FCSTD DOCUMENT  (FreeCAD 0.19R23546 (Git))
Label: PCB Reference
License: All rights reserved
LicenseURL: http://en.wikipedia.org/wiki/All_rights_reserved
objects: TechDraw::DrawViewDimension×22, TechDraw::DrawRichAnno×22, Spreadsheet::Sheet×1, Sketcher::SketchObject×1, PartDesign::Body×1, TechDraw::DrawSVGTemplate×1, TechDraw::DrawViewPart×1, TechDraw::DrawPage×1
note: 2 computed .brp shape members not serialized (recipe doc carries the construction recipe); baked Part::Feature solids carry a one-line shape summary decoded from their .brp

FEATURE [Spreadsheet::Sheet] Spreadsheet  label="Variables"
FEATURE [Sketcher::SketchObject] Sketch
  MapMode = 5
  Support = -> [XY_Plane]
  sketch-geometry (34):
    g0: LineSegment StartX=-33 StartY=-8.93934 StartZ=0 EndX=-31.9393 EndY=-10 EndZ=0
    g1: LineSegment StartX=-31.9393 StartY=-10 StartZ=0 EndX=31.9393 EndY=-10 EndZ=0
    g2: LineSegment StartX=31.9393 StartY=-10 StartZ=0 EndX=33 EndY=-8.93934 EndZ=0
    g3: LineSegment StartX=-33 StartY=-8.93934 StartZ=0 EndX=-33 EndY=6.93934 EndZ=0
    g4: LineSegment StartX=-33 StartY=6.93934 StartZ=0 EndX=-31.9393 EndY=8 EndZ=0
    g5: LineSegment StartX=33 StartY=-8.93934 StartZ=0 EndX=33 EndY=-2.56066 EndZ=0
    g6: LineSegment StartX=33 StartY=-2.56066 StartZ=0 EndX=31.9393 EndY=-1.5 EndZ=0
    g7: LineSegment StartX=-31.9393 StartY=8 StartZ=0 EndX=-28 EndY=8 EndZ=0
    g8: LineSegment StartX=24.9393 StartY=6.5 StartZ=0 EndX=-16 EndY=6.5 EndZ=0
    g9: LineSegment StartX=-16 StartY=6.5 StartZ=0 EndX=-19.5 EndY=10 EndZ=0
    g10: LineSegment StartX=-19.5 StartY=10 StartZ=0 EndX=-26 EndY=10 EndZ=0
    g11: LineSegment StartX=-26 StartY=10 StartZ=0 EndX=-28 EndY=8 EndZ=0
    g12: LineSegment StartX=24.9393 StartY=6.5 StartZ=0 EndX=26 EndY=5.43934 EndZ=0
    g13: LineSegment StartX=31.9393 StartY=-1.5 StartZ=0 EndX=26 EndY=-1.5 EndZ=0
    g14: LineSegment StartX=26 StartY=-1.5 StartZ=0 EndX=26 EndY=5.43934 EndZ=0
    g15: GeomPoint X=-19.5 Y=-10 Z=0
    g16: Circle CenterX=-29 CenterY=-5 CenterZ=0 NormalX=0 NormalY=0 NormalZ=1 AngleXU=0 Radius=2
    g17: Circle CenterX=29 CenterY=-5 CenterZ=0 NormalX=0 NormalY=0 NormalZ=1 AngleXU=0 Radius=2
    g18: LineSegment StartX=-32 StartY=5.5 StartZ=0 EndX=-26 EndY=5.5 EndZ=0
    g19: LineSegment StartX=-26 StartY=5.5 StartZ=0 EndX=-26 EndY=-0.5 EndZ=0
    g20: LineSegment StartX=-26 StartY=-0.5 StartZ=0 EndX=-32 EndY=-0.5 EndZ=0
    g21: LineSegment StartX=-32 StartY=-0.5 StartZ=0 EndX=-32 EndY=5.5 EndZ=0
    g22: GeomPoint X=-29 Y=2.5 Z=0
    g23: Circle CenterX=-22 CenterY=7.5 CenterZ=0 NormalX=0 NormalY=0 NormalZ=1 AngleXU=0 Radius=1.5
    g24: LineSegment StartX=-25 StartY=4.5 StartZ=0 EndX=25 EndY=4.5 EndZ=0
    g25: LineSegment StartX=25 StartY=4.5 StartZ=0 EndX=25 EndY=-0.5 EndZ=0
    g26: LineSegment StartX=25 StartY=-0.5 StartZ=0 EndX=-25 EndY=-0.5 EndZ=0
    g27: LineSegment StartX=-25 StartY=-0.5 StartZ=0 EndX=-25 EndY=4.5 EndZ=0
    g28: LineSegment StartX=-25 StartY=-2.5 StartZ=0 EndX=25 EndY=-2.5 EndZ=0
    g29: LineSegment StartX=25 StartY=-2.5 StartZ=0 EndX=25 EndY=-7.5 EndZ=0
    g30: LineSegment StartX=25 StartY=-7.5 StartZ=0 EndX=-25 EndY=-7.5 EndZ=0
    g31: LineSegment StartX=-25 StartY=-7.5 StartZ=0 EndX=-25 EndY=-2.5 EndZ=0
    g32: GeomPoint X=-5e-16 Y=-5 Z=0
    g33: GeomPoint X=-5e-16 Y=2 Z=0
  constraints (91):
    c: Coincident(g0,g1)
    c: Horizontal(g1)
    c: Coincident(g1,g2)
    c: DistanceX(g0,g2) = 66
    c: Coincident(g3,g0)
    c: Vertical(g3)
    c: Coincident(g4,g3)
    c: DistanceY(g0,g4) = 18
    c: Equal(g4,g0)
    c: Equal(g0,g2)
    c: Angle(g2,g1) = 2.35619
    c: Angle(g3,g4) = 2.35619
    c: Coincident(g5,g2)
    c: Vertical(g5)
    c: Coincident(g5,g6)
    c: Equal(g6,g2)
    c: Angle(g6,g5) = 2.35619
    c: DistanceY(g1,g6) = 8.5
    c: DistanceY(g1,g8) = 16.5
    c: Coincident(g7,g4)
    c: Horizontal(g7)
    c: Horizontal(g8)
    c: Coincident(g8,g9)
    c: Coincident(g9,g10)
    c: Horizontal(g10)
    c: Coincident(g10,g11)
    c: Coincident(g11,g7)
    c: Angle(g10,g9) = 2.35619
    c: Angle(g11,g10) = 2.35619
    c: DistanceY(g0,g10) = 20
    c: Coincident(g12,g8)
    c: Equal(g12,g6)
    c: Angle(g8,g12) = 2.35619
    c: Coincident(g6,g13)
    c: Horizontal(g13)
    c: Coincident(g14,g12)
    c: Vertical(g14)
    c: DistanceX(g3,g12) = 59
    c: DistanceX(g7,g12) = 54
    c: DistanceX(g8,g12) = 42
    c: Distance(g12) = 1.5
    c: Symmetric(g0,g2,g-2)
    c: Symmetric(g9,g15,g-1)
    c: Equal(g17,g16)
    c: Symmetric(g16,g17,g-2)
    c: DistanceX(g16,g17) = 58
    c: Diameter(g16) = 4
    c: Coincident(g18,g19)
    c: Coincident(g19,g20)
    c: Coincident(g20,g21)
    c: Coincident(g21,g18)
    c: Horizontal(g18)
    c: Horizontal(g20)
    c: Vertical(g19)
    c: Vertical(g21)
    c: Equal(g18,g21)
    c: Symmetric(g18,g20,g22)
    c: Vertical(g22,g16)
    c: PointOnObject(g15,g1)
    c: Diameter(g23) = 3
    c: Coincident(g24,g25)
    c: Coincident(g25,g26)
    c: Coincident(g26,g27)
    c: Coincident(g27,g24)
    c: Horizontal(g24)
    c: Horizontal(g26)
    c: Vertical(g25)
    c: Vertical(g27)
    c: Coincident(g28,g29)
    c: Coincident(g29,g30)
    c: Coincident(g30,g31)
    c: Coincident(g31,g28)
    c: Horizontal(g28)
    c: Horizontal(g30)
    c: Vertical(g29)
    c: Vertical(g31)
    c: Equal(g24,g28)
    c: Equal(g27,g31)
    c: DistanceX(g30,g30) = 50
    c: Symmetric(g26,g24,g33)
    c: Symmetric(g30,g28,g32)
    c: Vertical(g32,g33)
    c: Symmetric(g16,g17,g32)
    c: DistanceY(g16,g22) = 7.5
    c: DistanceY(g16,g23) = 12.5
    c: DistanceY(g16,g18) = 10.5
    c: DistanceX(g23,g12) = 48
    c: DistanceY(g28,g26) = 2
    c: DistanceY(g1,g24) = 14.5
    c: DistanceY(g29,g24) = 12
    c: Coincident(g14,g13)
FEATURE [PartDesign::Body] Body
  Group = -> [Sketch]
  Origin = -> Origin
FEATURE [TechDraw::DrawSVGTemplate] Template
  Height = 210
  Orientation = 1
  Width = 297
FEATURE [TechDraw::DrawViewPart] View  label="Pi Case 40 PCB"
  CoarseView = false
  Direction = (0,0,1)
  Focus = 100
  HardHidden = false
  IsoCount = 0
  IsoHidden = false
  IsoVisible = false
  LockPosition = false
  Perspective = false
  Rotation = 0
  Scale = 2.5
  ScaleType = 0
  SeamHidden = false
  SeamVisible = true
  SmoothHidden = false
  SmoothVisible = true
  Source = -> [Sketch]
  X = 152.053
  XDirection = (1,0,0)
  Y = 108.319
FEATURE [TechDraw::DrawViewDimension] Dimension
  Arbitrary = false
  ArbitraryTolerances = false
  FormatSpec = %.5f
  FormatSpecOverTolerance = %+.5f
  FormatSpecUnderTolerance = %+.5f
  Inverted = false
  LockPosition = false
  MeasureType = 1
  OverTolerance = 0
  References2D = -> [View]
  Rotation = 0
  ScaleType = 0
  TheoreticalExact = false
  Type = 1
  UnderTolerance = 0
  X = 2.44887
  Y = -79.5614
FEATURE [TechDraw::DrawViewDimension] Dimension001
  Arbitrary = false
  ArbitraryTolerances = false
  FormatSpec = %.5f
  FormatSpecOverTolerance = %+.5f
  FormatSpecUnderTolerance = %+.5f
  Inverted = false
  LockPosition = false
  MeasureType = 1
  OverTolerance = 0
  References2D = -> [View]
  Rotation = 0
  ScaleType = 0
  TheoreticalExact = false
  Type = 1
  UnderTolerance = 0
  X = -36.3768
  Y = -49.0906
FEATURE [TechDraw::DrawViewDimension] Dimension002
  Arbitrary = false
  ArbitraryTolerances = false
  FormatSpec = %.5f
  FormatSpecOverTolerance = %+.5f
  FormatSpecUnderTolerance = %+.5f
  Inverted = false
  LockPosition = false
  MeasureType = 1
  OverTolerance = 0
  References2D = -> [View]
  Rotation = 0
  ScaleType = 0
  TheoreticalExact = false
  Type = 2
  UnderTolerance = 0
  X = -107.499
  Y = -0.171562
FEATURE [TechDraw::DrawViewDimension] Dimension003
  Arbitrary = false
  ArbitraryTolerances = false
  FormatSpec = %.5f
  FormatSpecOverTolerance = %+.5f
  FormatSpecUnderTolerance = %+.5f
  Inverted = false
  LockPosition = false
  MeasureType = 1
  OverTolerance = 0
  References2D = -> [View]
  Rotation = 0
  ScaleType = 0
  TheoreticalExact = false
  Type = 2
  UnderTolerance = 0
  X = 11.4862
  Y = 42.3663
FEATURE [TechDraw::DrawViewDimension] Dimension004
  Arbitrary = false
  ArbitraryTolerances = false
  FormatSpec = %.5f
  FormatSpecOverTolerance = %+.5f
  FormatSpecUnderTolerance = %+.5f
  Inverted = false
  LockPosition = false
  MeasureType = 1
  OverTolerance = 0
  References2D = -> [View]
  Rotation = 0
  ScaleType = 0
  TheoreticalExact = false
  Type = 2
  UnderTolerance = 0
  X = -26.4883
  Y = 59.9243
FEATURE [TechDraw::DrawViewDimension] Dimension005
  Arbitrary = false
  ArbitraryTolerances = false
  FormatSpec = %.5f
  FormatSpecOverTolerance = %+.5f
  FormatSpecUnderTolerance = %+.5f
  Inverted = false
  LockPosition = false
  MeasureType = 1
  OverTolerance = 0
  References2D = -> [View]
  Rotation = 0
  ScaleType = 0
  TheoreticalExact = false
  Type = 1
  UnderTolerance = 0
  X = -135.209
  Y = 44.3895
FEATURE [TechDraw::DrawViewDimension] Dimension006
  Arbitrary = false
  ArbitraryTolerances = false
  FormatSpec = %.5f
  FormatSpecOverTolerance = %+.5f
  FormatSpecUnderTolerance = %+.5f
  Inverted = false
  LockPosition = false
  MeasureType = 1
  OverTolerance = 0
  References2D = -> [View]
  Rotation = 0
  ScaleType = 0
  TheoreticalExact = false
  Type = 1
  UnderTolerance = 0
  X = 110
  Y = -79.5614
FEATURE [TechDraw::DrawViewDimension] Dimension007
  Arbitrary = false
  ArbitraryTolerances = false
  FormatSpec = %.5f
  FormatSpecOverTolerance = %+.5f
  FormatSpecUnderTolerance = %+.5f
  Inverted = false
  LockPosition = false
  MeasureType = 1
  OverTolerance = 0
  References2D = -> [View]
  Rotation = 0
  ScaleType = 0
  TheoreticalExact = false
  Type = 1
  UnderTolerance = 0
  X = -110
  Y = -79.5614
FEATURE [TechDraw::DrawViewDimension] Dimension009  label="Dimension008"
  Arbitrary = false
  ArbitraryTolerances = false
  FormatSpec = %.5f
  FormatSpecOverTolerance = %+.5f
  FormatSpecUnderTolerance = %+.5f
  Inverted = false
  LockPosition = false
  MeasureType = 1
  OverTolerance = 0
  References2D = -> [View]
  Rotation = 0
  ScaleType = 0
  TheoreticalExact = false
  Type = 2
  UnderTolerance = 0
  X = 130.595
  Y = 28.7211
FEATURE [TechDraw::DrawViewDimension] Dimension010  label="Dimension009"
  Arbitrary = false
  ArbitraryTolerances = false
  FormatSpec = %.5f
  FormatSpecOverTolerance = %+.5f
  FormatSpecUnderTolerance = %+.5f
  Inverted = false
  LockPosition = false
  MeasureType = 1
  OverTolerance = 0
  References2D = -> [View]
  Rotation = 0
  ScaleType = 0
  TheoreticalExact = false
  Type = 2
  UnderTolerance = 0
  X = -24.2481
  Y = -32.564
FEATURE [TechDraw::DrawViewDimension] Dimension012  label="Dimension010"
  Arbitrary = false
  ArbitraryTolerances = false
  FormatSpec = ⌀%.5f
  FormatSpecOverTolerance = %+.5f
  FormatSpecUnderTolerance = %+.5f
  Inverted = false
  LockPosition = false
  MeasureType = 1
  OverTolerance = 0
  References2D = -> [View]
  Rotation = 0
  ScaleType = 0
  TheoreticalExact = false
  Type = 5
  UnderTolerance = 0
  X = -99.8906
  Y = 34.5564
FEATURE [TechDraw::DrawViewDimension] Dimension013  label="Dimension011"
  Arbitrary = false
  ArbitraryTolerances = false
  FormatSpec = ⌀%.5f
  FormatSpecOverTolerance = %+.5f
  FormatSpecUnderTolerance = %+.5f
  Inverted = false
  LockPosition = false
  MeasureType = 1
  OverTolerance = 0
  References2D = -> [View]
  Rotation = 0
  ScaleType = 0
  TheoreticalExact = false
  Type = 5
  UnderTolerance = 0
  X = -126.755
  Y = -35.391
FEATURE [TechDraw::DrawViewDimension] Dimension014  label="Dimension012"
  Arbitrary = false
  ArbitraryTolerances = false
  FormatSpec = %.5f
  FormatSpecOverTolerance = %+.5f
  FormatSpecUnderTolerance = %+.5f
  Inverted = false
  LockPosition = false
  MeasureType = 1
  OverTolerance = 0
  References2D = -> [View]
  Rotation = 0
  ScaleType = 0
  TheoreticalExact = false
  Type = 1
  UnderTolerance = 0
  X = -101.214
  Y = 16.3698
FEATURE [TechDraw::DrawViewDimension] Dimension015  label="Dimension013"
  Arbitrary = false
  ArbitraryTolerances = false
  FormatSpec = %.5f
  FormatSpecOverTolerance = %+.5f
  FormatSpecUnderTolerance = %+.5f
  Inverted = false
  LockPosition = false
  MeasureType = 1
  OverTolerance = 0
  References2D = -> [View]
  Rotation = 0
  ScaleType = 0
  TheoreticalExact = false
  Type = 1
  UnderTolerance = 0
  X = 117.642
  Y = 51.0013
FEATURE [TechDraw::DrawViewDimension] Dimension017  label="Dimension014"
  Arbitrary = false
  ArbitraryTolerances = false
  FormatSpec = %.5f
  FormatSpecOverTolerance = %+.5f
  FormatSpecUnderTolerance = %+.5f
  Inverted = false
  LockPosition = false
  MeasureType = 1
  OverTolerance = 0
  References2D = -> [View]
  Rotation = 0
  ScaleType = 0
  TheoreticalExact = false
  Type = 2
  UnderTolerance = 0
  X = -10.0565
  Y = 47.3314
FEATURE [TechDraw::DrawViewDimension] Dimension018  label="Dimension015"
  Arbitrary = false
  ArbitraryTolerances = false
  FormatSpec = %.5f
  FormatSpecOverTolerance = %+.5f
  FormatSpecUnderTolerance = %+.5f
  Inverted = false
  LockPosition = false
  MeasureType = 1
  OverTolerance = 0
  References2D = -> [View]
  Rotation = 0
  ScaleType = 0
  TheoreticalExact = false
  Type = 1
  UnderTolerance = 0
  X = 0.502827
  Y = -66.5186
FEATURE [TechDraw::DrawViewDimension] Dimension019  label="Dimension016"
  Arbitrary = false
  ArbitraryTolerances = false
  FormatSpec = %.5f
  FormatSpecOverTolerance = %+.5f
  FormatSpecUnderTolerance = %+.5f
  Inverted = false
  LockPosition = false
  MeasureType = 1
  OverTolerance = 0
  References2D = -> [View]
  Rotation = 0
  ScaleType = 0
  TheoreticalExact = false
  Type = 2
  UnderTolerance = 0
  X = -56.0203
  Y = -32.2427
FEATURE [TechDraw::DrawViewDimension] Dimension020  label="Dimension017"
  Arbitrary = false
  ArbitraryTolerances = false
  FormatSpec = %.5f
  FormatSpecOverTolerance = %+.5f
  FormatSpecUnderTolerance = %+.5f
  Inverted = false
  LockPosition = false
  MeasureType = 1
  OverTolerance = 0
  References2D = -> [View]
  Rotation = 0
  ScaleType = 0
  TheoreticalExact = false
  Type = 2
  UnderTolerance = 0
  X = -121.322
  Y = -12.3701
FEATURE [TechDraw::DrawViewDimension] Dimension022  label="Dimension018"
  Arbitrary = false
  ArbitraryTolerances = false
  FormatSpec = %.5f
  FormatSpecOverTolerance = %+.5f
  FormatSpecUnderTolerance = %+.5f
  Inverted = false
  LockPosition = false
  MeasureType = 1
  OverTolerance = 0
  References2D = -> [View]
  Rotation = 0
  ScaleType = 0
  TheoreticalExact = false
  Type = 1
  UnderTolerance = 0
  X = -134.545
  Y = 59.7561
FEATURE [TechDraw::DrawViewDimension] Dimension023  label="Dimension019"
  Arbitrary = false
  ArbitraryTolerances = false
  FormatSpec = %.5f
  FormatSpecOverTolerance = %+.5f
  FormatSpecUnderTolerance = %+.5f
  Inverted = false
  LockPosition = false
  MeasureType = 1
  OverTolerance = 0
  References2D = -> [View]
  Rotation = 0
  ScaleType = 0
  TheoreticalExact = false
  Type = 2
  UnderTolerance = 0
  X = -47.2825
  Y = 72.776
FEATURE [TechDraw::DrawViewDimension] Dimension024  label="Dimension020"
  Arbitrary = false
  ArbitraryTolerances = false
  FormatSpec = %.5f
  FormatSpecOverTolerance = %+.5f
  FormatSpecUnderTolerance = %+.5f
  Inverted = false
  LockPosition = false
  MeasureType = 1
  OverTolerance = 0
  References2D = -> [View]
  Rotation = 0
  ScaleType = 0
  TheoreticalExact = false
  Type = 1
  UnderTolerance = 0
  X = -11.464
  Y = 91.4575
FEATURE [TechDraw::DrawViewDimension] Dimension025  label="Dimension021"
  Arbitrary = false
  ArbitraryTolerances = false
  FormatSpec = %.5f
  FormatSpecOverTolerance = %+.5f
  FormatSpecUnderTolerance = %+.5f
  Inverted = false
  LockPosition = false
  MeasureType = 1
  OverTolerance = 0
  References2D = -> [View]
  Rotation = 0
  ScaleType = 0
  TheoreticalExact = false
  Type = 2
  UnderTolerance = 0
  X = 29.4625
  Y = 37.9035
FEATURE [TechDraw::DrawRichAnno] RichTextAnnotation
  AnnoText = <!DOCTYPE HTML PUBLIC "-//W3C//DTD HTML 4.0//EN" "http://www.w3.org/TR/REC-html40/strict.dtd">\n<html><head><meta name="qrichtext" content="1" /><style type="text/css">\np, li { white-space: pre-wrap; }\n</style></head><body style=" font-family:'Sans Serif'; font-size:9pt; font-weight:400; font-style:normal;">\n<p style=" margin-top:0px; margin-bottom:0px; margin-left:0px; margin-right:0px; -qt-block-indent:0; text-indent:0px;"><span style=" font-size:10pt;">A</span></p></body></html>
  LockPosition = false
  MaxWidth = -1
  Rotation = 0
  ScaleType = 0
  ShowFrame = true
  X = 12.8703
  Y = 64.9892
FEATURE [TechDraw::DrawRichAnno] RichTextAnnotation001
  AnnoText = <!DOCTYPE HTML PUBLIC "-//W3C//DTD HTML 4.0//EN" "http://www.w3.org/TR/REC-html40/strict.dtd">\n<html><head><meta name="qrichtext" content="1" /><style type="text/css">\np, li { white-space: pre-wrap; }\n</style></head><body style=" font-family:'Sans Serif'; font-size:9pt; font-weight:400; font-style:normal;">\n<p style=" margin-top:0px; margin-bottom:0px; margin-left:0px; margin-right:0px; -qt-block-indent:0; text-indent:0px;"><span style=" font-size:10pt;">B</span></p></body></html>
  LockPosition = false
  MaxWidth = -1
  Rotation = 0
  ScaleType = 0
  ShowFrame = true
  X = 143.55
  Y = 26.9592
FEATURE [TechDraw::DrawRichAnno] RichTextAnnotation002
  AnnoText = <!DOCTYPE HTML PUBLIC "-//W3C//DTD HTML 4.0//EN" "http://www.w3.org/TR/REC-html40/strict.dtd">\n<html><head><meta name="qrichtext" content="1" /><style type="text/css">\np, li { white-space: pre-wrap; }\n</style></head><body style=" font-family:'Sans Serif'; font-size:9pt; font-weight:400; font-style:normal;">\n<p style=" margin-top:0px; margin-bottom:0px; margin-left:0px; margin-right:0px; -qt-block-indent:0; text-indent:0px;"><span style=" font-size:10pt;">C</span></p></body></html>
  LockPosition = false
  MaxWidth = -1
  Rotation = 0
  ScaleType = 0
  ShowFrame = true
  X = 141.773
  Y = 39.596
FEATURE [TechDraw::DrawRichAnno] RichTextAnnotation003
  AnnoText = <!DOCTYPE HTML PUBLIC "-//W3C//DTD HTML 4.0//EN" "http://www.w3.org/TR/REC-html40/strict.dtd">\n<html><head><meta name="qrichtext" content="1" /><style type="text/css">\np, li { white-space: pre-wrap; }\n</style></head><body style=" font-family:'Sans Serif'; font-size:9pt; font-weight:400; font-style:normal;">\n<p style=" margin-top:0px; margin-bottom:0px; margin-left:0px; margin-right:0px; -qt-block-indent:0; text-indent:0px;"><span style=" font-size:10pt;">D</span></p></body></html>
  LockPosition = false
  MaxWidth = -1
  Rotation = 0
  ScaleType = 0
  ShowFrame = true
  X = 95.9555
  Y = 62.0234
FEATURE [TechDraw::DrawRichAnno] RichTextAnnotation004
  AnnoText = <!DOCTYPE HTML PUBLIC "-//W3C//DTD HTML 4.0//EN" "http://www.w3.org/TR/REC-html40/strict.dtd">\n<html><head><meta name="qrichtext" content="1" /><style type="text/css">\np, li { white-space: pre-wrap; }\n</style></head><body style=" font-family:'Sans Serif'; font-size:9pt; font-weight:400; font-style:normal;">\n<p style=" margin-top:0px; margin-bottom:0px; margin-left:0px; margin-right:0px; -qt-block-indent:0; text-indent:0px;"><span style=" font-size:10pt;">E</span></p></body></html>
  LockPosition = false
  MaxWidth = -1
  Rotation = 0
  ScaleType = 0
  ShowFrame = true
  X = 127.929
  Y = 62.5027
FEATURE [TechDraw::DrawRichAnno] RichTextAnnotation005
  AnnoText = <!DOCTYPE HTML PUBLIC "-//W3C//DTD HTML 4.0//EN" "http://www.w3.org/TR/REC-html40/strict.dtd">\n<html><head><meta name="qrichtext" content="1" /><style type="text/css">\np, li { white-space: pre-wrap; }\n</style></head><body style=" font-family:'Sans Serif'; font-size:9pt; font-weight:400; font-style:normal;">\n<p style=" margin-top:0px; margin-bottom:0px; margin-left:0px; margin-right:0px; -qt-block-indent:0; text-indent:0px;"><span style=" font-size:10pt;">F</span></p></body></html>
  LockPosition = false
  MaxWidth = -1
  Rotation = 0
  ScaleType = 0
  ShowFrame = true
  X = 104.684
  Y = 57.4166
FEATURE [TechDraw::DrawRichAnno] RichTextAnnotation006
  AnnoText = <!DOCTYPE HTML PUBLIC "-//W3C//DTD HTML 4.0//EN" "http://www.w3.org/TR/REC-html40/strict.dtd">\n<html><head><meta name="qrichtext" content="1" /><style type="text/css">\np, li { white-space: pre-wrap; }\n</style></head><body style=" font-family:'Sans Serif'; font-size:9pt; font-weight:400; font-style:normal;">\n<p style=" margin-top:0px; margin-bottom:0px; margin-left:0px; margin-right:0px; -qt-block-indent:0; text-indent:0px;"><span style=" font-size:10pt;">G</span></p></body></html>
  LockPosition = false
  MaxWidth = -1
  Rotation = 0
  ScaleType = 0
  ShowFrame = true
  X = 163.043
  Y = 137.061
FEATURE [TechDraw::DrawRichAnno] RichTextAnnotation007
  AnnoText = <!DOCTYPE HTML PUBLIC "-//W3C//DTD HTML 4.0//EN" "http://www.w3.org/TR/REC-html40/strict.dtd">\n<html><head><meta name="qrichtext" content="1" /><style type="text/css">\np, li { white-space: pre-wrap; }\n</style></head><body style=" font-family:'Sans Serif'; font-size:9pt; font-weight:400; font-style:normal;">\n<p style=" margin-top:0px; margin-bottom:0px; margin-left:0px; margin-right:0px; -qt-block-indent:0; text-indent:0px;"><span style=" font-size:10pt;">H</span></p></body></html>
  LockPosition = false
  MaxWidth = -1
  Rotation = 0
  ScaleType = 0
  ShowFrame = true
  X = 40.5099
  Y = 121.84
FEATURE [TechDraw::DrawRichAnno] RichTextAnnotation008
  AnnoText = <!DOCTYPE HTML PUBLIC "-//W3C//DTD HTML 4.0//EN" "http://www.w3.org/TR/REC-html40/strict.dtd">\n<html><head><meta name="qrichtext" content="1" /><style type="text/css">\np, li { white-space: pre-wrap; }\n</style></head><body style=" font-family:'Sans Serif'; font-size:9pt; font-weight:400; font-style:normal;">\n<p style=" margin-top:0px; margin-bottom:0px; margin-left:0px; margin-right:0px; -qt-block-indent:0; text-indent:0px;"><span style=" font-size:10pt;">I</span></p></body></html>
  LockPosition = false
  MaxWidth = -1
  Rotation = 0
  ScaleType = 0
  ShowFrame = true
  X = 43.7949
  Y = 94.7576
FEATURE [TechDraw::DrawRichAnno] RichTextAnnotation009
  AnnoText = <!DOCTYPE HTML PUBLIC "-//W3C//DTD HTML 4.0//EN" "http://www.w3.org/TR/REC-html40/strict.dtd">\n<html><head><meta name="qrichtext" content="1" /><style type="text/css">\np, li { white-space: pre-wrap; }\n</style></head><body style=" font-family:'Sans Serif'; font-size:9pt; font-weight:400; font-style:normal;">\n<p style=" margin-top:0px; margin-bottom:0px; margin-left:0px; margin-right:0px; -qt-block-indent:0; text-indent:0px;"><span style=" font-size:10pt;">J</span></p></body></html>
  LockPosition = false
  MaxWidth = -1
  Rotation = 0
  ScaleType = 0
  ShowFrame = true
  X = 41.3887
  Y = 141.684
FEATURE [TechDraw::DrawRichAnno] RichTextAnnotation010
  AnnoText = <!DOCTYPE HTML PUBLIC "-//W3C//DTD HTML 4.0//EN" "http://www.w3.org/TR/REC-html40/strict.dtd">\n<html><head><meta name="qrichtext" content="1" /><style type="text/css">\np, li { white-space: pre-wrap; }\n</style></head><body style=" font-family:'Sans Serif'; font-size:9pt; font-weight:400; font-style:normal;">\n<p style=" margin-top:0px; margin-bottom:0px; margin-left:0px; margin-right:0px; -qt-block-indent:0; text-indent:0px;"><span style=" font-size:10pt;">K</span></p></body></html>
  LockPosition = false
  MaxWidth = -1
  Rotation = 0
  ScaleType = 0
  ShowFrame = true
  X = 7.09069
  Y = 149.921
FEATURE [TechDraw::DrawRichAnno] RichTextAnnotation011
  AnnoText = <!DOCTYPE HTML PUBLIC "-//W3C//DTD HTML 4.0//EN" "http://www.w3.org/TR/REC-html40/strict.dtd">\n<html><head><meta name="qrichtext" content="1" /><style type="text/css">\np, li { white-space: pre-wrap; }\n</style></head><body style=" font-family:'Sans Serif'; font-size:9pt; font-weight:400; font-style:normal;">\n<p style=" margin-top:0px; margin-bottom:0px; margin-left:0px; margin-right:0px; -qt-block-indent:0; text-indent:0px;"><span style=" font-size:10pt;">L</span></p></body></html>
  LockPosition = false
  MaxWidth = -1
  Rotation = 0
  ScaleType = 0
  ShowFrame = true
  X = 125.663
  Y = 155.021
FEATURE [TechDraw::DrawRichAnno] RichTextAnnotation012
  AnnoText = <!DOCTYPE HTML PUBLIC "-//W3C//DTD HTML 4.0//EN" "http://www.w3.org/TR/REC-html40/strict.dtd">\n<html><head><meta name="qrichtext" content="1" /><style type="text/css">\np, li { white-space: pre-wrap; }\n</style></head><body style=" font-family:'Sans Serif'; font-size:9pt; font-weight:400; font-style:normal;">\n<p style=" margin-top:0px; margin-bottom:0px; margin-left:0px; margin-right:0px; -qt-block-indent:0; text-indent:0px;"><span style=" font-size:10pt;">M</span></p></body></html>
  LockPosition = false
  MaxWidth = -1
  Rotation = 0
  ScaleType = 0
  ShowFrame = true
  X = 31.2557
  Y = 25.958
FEATURE [TechDraw::DrawRichAnno] RichTextAnnotation013
  AnnoText = <!DOCTYPE HTML PUBLIC "-//W3C//DTD HTML 4.0//EN" "http://www.w3.org/TR/REC-html40/strict.dtd">\n<html><head><meta name="qrichtext" content="1" /><style type="text/css">\np, li { white-space: pre-wrap; }\n</style></head><body style=" font-family:'Sans Serif'; font-size:9pt; font-weight:400; font-style:normal;">\n<p style=" margin-top:0px; margin-bottom:0px; margin-left:0px; margin-right:0px; -qt-block-indent:0; text-indent:0px;"><span style=" font-size:10pt;">N</span></p></body></html>
  LockPosition = false
  MaxWidth = -1
  Rotation = 0
  ScaleType = 0
  ShowFrame = true
  X = 251.88
  Y = 26.0334
FEATURE [TechDraw::DrawRichAnno] RichTextAnnotation014
  AnnoText = <!DOCTYPE HTML PUBLIC "-//W3C//DTD HTML 4.0//EN" "http://www.w3.org/TR/REC-html40/strict.dtd">\n<html><head><meta name="qrichtext" content="1" /><style type="text/css">\np, li { white-space: pre-wrap; }\n</style></head><body style=" font-family:'Sans Serif'; font-size:9pt; font-weight:400; font-style:normal;">\n<p style=" margin-top:0px; margin-bottom:0px; margin-left:0px; margin-right:0px; -qt-block-indent:0; text-indent:0px;"><span style=" font-size:10pt;">O</span></p></body></html>
  LockPosition = false
  MaxWidth = -1
  Rotation = 0
  ScaleType = 0
  ShowFrame = true
  X = 282.284
  Y = 123.687
FEATURE [TechDraw::DrawRichAnno] RichTextAnnotation015
  AnnoText = <!DOCTYPE HTML PUBLIC "-//W3C//DTD HTML 4.0//EN" "http://www.w3.org/TR/REC-html40/strict.dtd">\n<html><head><meta name="qrichtext" content="1" /><style type="text/css">\np, li { white-space: pre-wrap; }\n</style></head><body style=" font-family:'Sans Serif'; font-size:9pt; font-weight:400; font-style:normal;">\n<p style=" margin-top:0px; margin-bottom:0px; margin-left:0px; margin-right:0px; -qt-block-indent:0; text-indent:0px;"><span style=" font-size:10pt;">P</span></p></body></html>
  LockPosition = false
  MaxWidth = -1
  Rotation = 0
  ScaleType = 0
  ShowFrame = true
  X = 259.792
  Y = 156.599
FEATURE [TechDraw::DrawRichAnno] RichTextAnnotation016
  AnnoText = <!DOCTYPE HTML PUBLIC "-//W3C//DTD HTML 4.0//EN" "http://www.w3.org/TR/REC-html40/strict.dtd">\n<html><head><meta name="qrichtext" content="1" /><style type="text/css">\np, li { white-space: pre-wrap; }\n</style></head><body style=" font-family:'Sans Serif'; font-size:9pt; font-weight:400; font-style:normal;">\n<p style=" margin-top:0px; margin-bottom:0px; margin-left:0px; margin-right:0px; -qt-block-indent:0; text-indent:0px;"><span style=" font-size:10pt;">Q</span></p></body></html>
  LockPosition = false
  MaxWidth = -1
  Rotation = 0
  ScaleType = 0
  ShowFrame = true
  X = 30.2005
  Y = 82.8199
FEATURE [TechDraw::DrawRichAnno] RichTextAnnotation017
  AnnoText = <!DOCTYPE HTML PUBLIC "-//W3C//DTD HTML 4.0//EN" "http://www.w3.org/TR/REC-html40/strict.dtd">\n<html><head><meta name="qrichtext" content="1" /><style type="text/css">\np, li { white-space: pre-wrap; }\n</style></head><body style=" font-family:'Sans Serif'; font-size:9pt; font-weight:400; font-style:normal;">\n<p style=" margin-top:0px; margin-bottom:0px; margin-left:0px; margin-right:0px; -qt-block-indent:0; text-indent:0px;"><span style=" font-size:10pt;">R</span></p></body></html>
  LockPosition = false
  MaxWidth = -1
  Rotation = 0
  ScaleType = 0
  ShowFrame = true
  X = 7.81
  Y = 165.194
FEATURE [TechDraw::DrawRichAnno] RichTextAnnotation018
  AnnoText = <!DOCTYPE HTML PUBLIC "-//W3C//DTD HTML 4.0//EN" "http://www.w3.org/TR/REC-html40/strict.dtd">\n<html><head><meta name="qrichtext" content="1" /><style type="text/css">\np, li { white-space: pre-wrap; }\n</style></head><body style=" font-family:'Sans Serif'; font-size:9pt; font-weight:400; font-style:normal;">\n<p style=" margin-top:0px; margin-bottom:0px; margin-left:0px; margin-right:0px; -qt-block-indent:0; text-indent:0px;"><span style=" font-size:10pt;">S</span></p></body></html>
  LockPosition = false
  MaxWidth = -1
  Rotation = 0
  ScaleType = 0
  ShowFrame = true
  X = 141.627
  Y = 141.582
FEATURE [TechDraw::DrawRichAnno] RichTextAnnotation019
  AnnoText = <!DOCTYPE HTML PUBLIC "-//W3C//DTD HTML 4.0//EN" "http://www.w3.org/TR/REC-html40/strict.dtd">\n<html><head><meta name="qrichtext" content="1" /><style type="text/css">\np, li { white-space: pre-wrap; }\n</style></head><body style=" font-family:'Sans Serif'; font-size:9pt; font-weight:400; font-style:normal;">\n<p style=" margin-top:0px; margin-bottom:0px; margin-left:0px; margin-right:0px; -qt-block-indent:0; text-indent:0px;"><span style=" font-size:10pt;">T</span></p></body></html>
  LockPosition = false
  MaxWidth = -1
  Rotation = 0
  ScaleType = 0
  ShowFrame = true
  X = 104.631
  Y = 167.556
FEATURE [TechDraw::DrawRichAnno] RichTextAnnotation020
  AnnoText = <!DOCTYPE HTML PUBLIC "-//W3C//DTD HTML 4.0//EN" "http://www.w3.org/TR/REC-html40/strict.dtd">\n<html><head><meta name="qrichtext" content="1" /><style type="text/css">\np, li { white-space: pre-wrap; }\n</style></head><body style=" font-family:'Sans Serif'; font-size:9pt; font-weight:400; font-style:normal;">\n<p style=" margin-top:0px; margin-bottom:0px; margin-left:0px; margin-right:0px; -qt-block-indent:0; text-indent:0px;"><span style=" font-size:10pt;">U</span></p></body></html>
  LockPosition = false
  MaxWidth = -1
  Rotation = 0
  ScaleType = 0
  ShowFrame = true
  X = 130.01
  Y = 196.902
FEATURE [TechDraw::DrawRichAnno] RichTextAnnotation021
  AnnoText = <!DOCTYPE HTML PUBLIC "-//W3C//DTD HTML 4.0//EN" "http://www.w3.org/TR/REC-html40/strict.dtd">\n<html><head><meta name="qrichtext" content="1" /><style type="text/css">\np, li { white-space: pre-wrap; }\n</style></head><body style=" font-family:'Sans Serif'; font-size:9pt; font-weight:400; font-style:normal;">\n<p style=" margin-top:0px; margin-bottom:0px; margin-left:0px; margin-right:0px; -qt-block-indent:0; text-indent:0px;"><span style=" font-size:10pt;">V</span></p></body></html>
  LockPosition = false
  MaxWidth = -1
  Rotation = 0
  ScaleType = 0
  ShowFrame = true
  X = 181.445
  Y = 132.608
FEATURE [TechDraw::DrawPage] Page
  KeepUpdated = true
  NextBalloonIndex = 1
  ProjectionType = 0
  Template = -> Template
  Views = -> [View,Dimension,Dimension001,Dimension002,Dimension003,Dimension004,Dimension005,Dimension006,Dimension007,Dimension009,Dimension010,Dimension012,Dimension013,Dimension014,Dimension015,Dimension017,Dimension018,Dimension019,Dimension020,Dimension022,Dimension023,Dimension024,Dimension025,RichTextAnnotation,RichTextAnnotation001,RichTextAnnotation002,RichTextAnnotation003,RichTextAnnotation004,+17 more]
